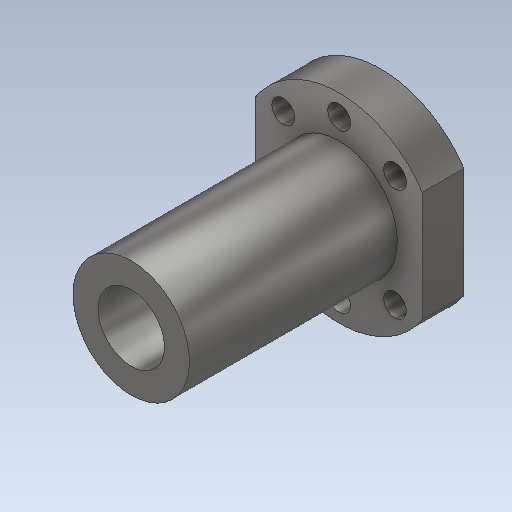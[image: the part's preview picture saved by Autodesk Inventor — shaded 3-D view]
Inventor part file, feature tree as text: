
AUTODESK INVENTOR PART (.ipt)
format: ipt  version: 2020 (Build 240168000, 168)  size: 182,784 bytes
history: native  units: mm
features: extrude x5, sketch x5, other x1, mirror x1
ambient origin geometry x8: Origin, YZ Plane, XZ Plane, XY Plane, X Axis, Y Axis, Z Axis, Center Point
bodies: Body1 (feature_tree)
feature tree (12):
  other  "Bryła1"
  extrude  "Wyciągnięcie proste1"  Depth=48.0mm
  extrude  "Wyciągnięcie proste2"  Depth=10.0mm TaperAngle=0.0deg
  extrude  "Wyciągnięcie proste3"  Depth=28.0mm
  extrude  "Wyciągnięcie proste4"  Depth=50.0mm TaperAngle=0.0deg
  extrude  "Wyciągnięcie proste5"  Depth=16.0mm
  mirror  "Odbij1"
  sketch  "Szkic1"
  sketch  "Szkic2"
  sketch  "Szkic3"
  sketch  "Szkic4"
  sketch  "Szkic5"
